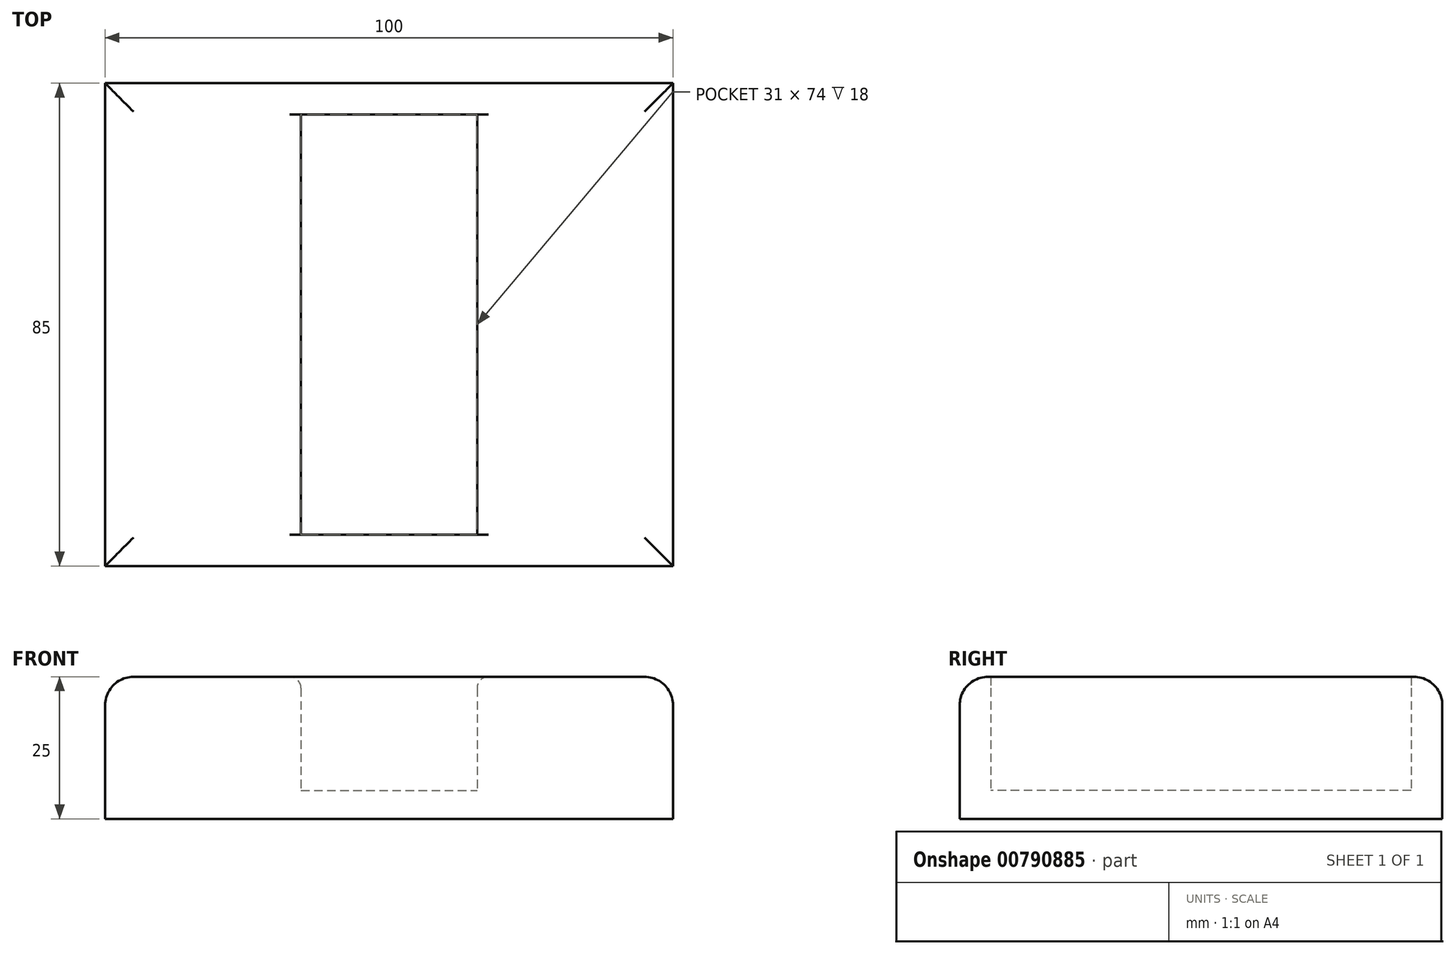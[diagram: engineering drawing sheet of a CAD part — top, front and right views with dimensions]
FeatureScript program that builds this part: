
annotation { "Feature Type Name" : "Feature", "Feature Type Description" : "" }
export const myFeature = defineFeature(function(context is Context, id is Id, definition is map)
    precondition{}
    {
        {
            var Q0;
            Q0=qCreatedBy(makeId("Top.planeOp"),FACE);
            var sketch = newSketch(context, id + "F0", { "sketchPlane" : qUnion([Q0])});
            skLineSegment(sketch, "E0.bottom", {"start": v(-50, 42.5) * mm, "end": v(50, 42.5) * mm});
            skLineSegment(sketch, "E0.top", {"start": v(-50, -42.5) * mm, "end": v(50, -42.5) * mm});
            skLineSegment(sketch, "E0.left", {"start": v(-50, 42.5) * mm, "end": v(-50, -42.5) * mm});
            skLineSegment(sketch, "E0.right", {"start": v(50, 42.5) * mm, "end": v(50, -42.5) * mm});
            skPoint(sketch, "E0.middle", {"position": v(0, 0) * mm});
            skLineSegment(sketch, "E1.bottom", {"start": v(-15.5, 37) * mm, "end": v(15.5, 37) * mm});
            skLineSegment(sketch, "E1.top", {"start": v(-15.5, -37) * mm, "end": v(15.5, -37) * mm});
            skLineSegment(sketch, "E1.left", {"start": v(-15.5, 37) * mm, "end": v(-15.5, -37) * mm});
            skLineSegment(sketch, "E1.right", {"start": v(15.5, 37) * mm, "end": v(15.5, -37) * mm});
            skSolve(sketch);
        }
        {
            var Q0;
            Q0=makeQuery(id+"F0.imprint","IMPRINT",FACE,{"disambiguationData":[TD([[makeQuery(id+"F0.imprint","IMPRINT",EDGE,{"derivedFrom":sQuery(id+"F0.wireOp",EDGE,"E0.bottom")}),-1.0]])]});
            extrude(context, id + "F1", {"entities" : qUnion([Q0]), "depth" : 25 * mm, "offsetDistance" : 25 * mm});
        }
        {
            var Q0;
            Q0=makeQuery(id+"F0.imprint","IMPRINT",FACE,{"disambiguationData":[TD([[makeQuery(id+"F0.imprint","IMPRINT",EDGE,{"derivedFrom":sQuery(id+"F0.wireOp",EDGE,"E1.bottom")}),-1.0]])]});
            extrude(context, id + "F2", {"entities" : qUnion([Q0]), "operationType" : NewBodyOperationType.ADD, "depth" : 5 * mm, "offsetDistance" : 25 * mm});
        }
        {
            var Q0;
            Q0=makeQuery(id+"F1.opExtrude","CAP_EDGE",EDGE,{"disambiguationData":[OSD([sQuery(id+"F0.wireOp",EDGE,"E0.bottom")])],"isStart":false});
            var Q1;
            Q1=makeQuery(id+"F1.opExtrude","CAP_EDGE",EDGE,{"disambiguationData":[OSD([sQuery(id+"F0.wireOp",EDGE,"E0.left")])],"isStart":false});
            var Q2;
            Q2=makeQuery(id+"F1.opExtrude","CAP_EDGE",EDGE,{"disambiguationData":[OSD([sQuery(id+"F0.wireOp",EDGE,"E0.top")])],"isStart":false});
            var Q3;
            Q3=makeQuery(id+"F1.opExtrude","CAP_EDGE",EDGE,{"disambiguationData":[OSD([sQuery(id+"F0.wireOp",EDGE,"E0.right")])],"isStart":false});
            fillet(context, id + "F3", {"entities" : qUnion([Q0, Q1, Q2, Q3]), "radius" : 5 * mm, "tangentPropagation" : true, "allowEdgeOverflow" : false});
        }
        {
            var Q0;
            Q0=makeQuery(id+"F1.opExtrude","CAP_EDGE",EDGE,{"disambiguationData":[OSD([sQuery(id+"F0.wireOp",EDGE,"E1.left")])],"isStart":false});
            var Q1;
            Q1=makeQuery(id+"F1.opExtrude","CAP_EDGE",EDGE,{"disambiguationData":[OSD([sQuery(id+"F0.wireOp",EDGE,"E1.right")])],"isStart":false});
            fillet(context, id + "F4", {"entities" : qUnion([Q0, Q1]), "radius" : 2 * mm, "tangentPropagation" : true, "allowEdgeOverflow" : false});
        }
    });
